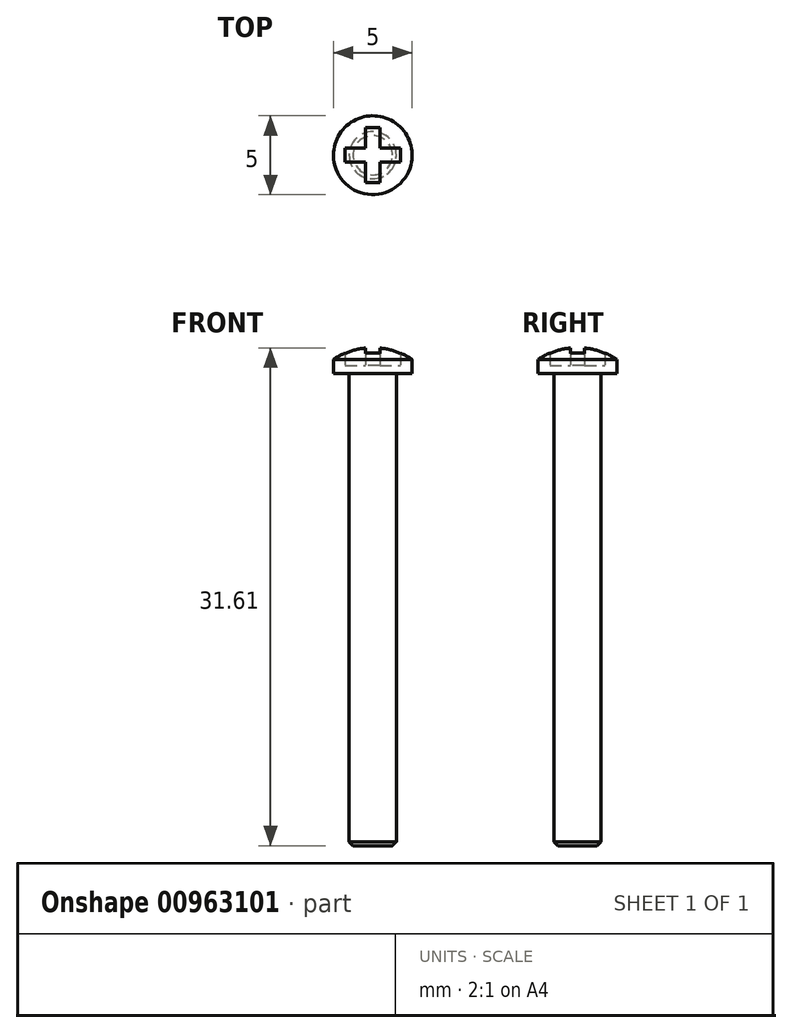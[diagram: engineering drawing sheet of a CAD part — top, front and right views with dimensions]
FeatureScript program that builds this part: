
annotation { "Feature Type Name" : "Feature", "Feature Type Description" : "" }
export const myFeature = defineFeature(function(context is Context, id is Id, definition is map)
    precondition{}
    {
        {
            var Q0;
            Q0=qCreatedBy(makeId("Front.planeOp"),FACE);
            var sketch = newSketch(context, id + "F0", { "sketchPlane" : qUnion([Q0])});
            skLineSegment(sketch, "E0", {"start": v(-1.5, 0) * mm, "end": v(-2.5, 0) * mm});
            skLineSegment(sketch, "E1", {"start": v(-2.5, 0) * mm, "end": v(-2.5, 0.88) * mm});
            skLineSegment(sketch, "E2", {"start": v(-1.5, 0) * mm, "end": v(-1.5, -30) * mm});
            skLineSegment(sketch, "E3", {"start": v(-1.5, -30) * mm, "end": v(0, -30) * mm});
            skLineSegment(sketch, "E4", {"start": v(0, -30) * mm, "end": v(0, 1.66) * mm});
            skArc(sketch, "E5", {"start": v(0, 1.66) * mm, "mid": v(-1.3, 1.46) * mm, "end": v(-2.5, 0.88) * mm});
            skSolve(sketch);
        }
        {
            var Q0;
            Q0 = qSketchRegion(id + "F0", true);
            var Q1;
            Q1=sQuery(id+"F0.wireOp",EDGE,"E4");
            revolve(context, id + "F1", {"surfaceOperationType" : NewSurfaceOperationType.NEW, "entities" : qUnion([Q0]), "axis" : qUnion([Q1]), "revolveType" : RevolveType.FULL});
        }
        {
            var Q0;
            Q0=makeQuery(id+"F1.opRevolve","SWEPT_EDGE",EDGE,{"disambiguationData":[OSD([sQuery(id+"F0.wireOp",EDGE,"E2"),sQuery(id+"F0.wireOp",EDGE,"E3")])]});
            chamfer(context, id + "F2", {"entities" : qUnion([Q0]), "width" : 0.25 * mm, "tangentPropagation" : true});
        }
        {
            var Q0;
            Q0=qCreatedBy(makeId("Top.planeOp"),FACE);
            cPlane(context, id + "F3", {"entities" : qUnion([Q0]), "cplaneType" : CPlaneType.OFFSET, "offset" : 0.5 * mm, "width" : 150 * mm, "height" : 150 * mm});
        }
        {
            var Q0;
            Q0=qCreatedBy(id+"F3.planeOp",FACE);
            var sketch = newSketch(context, id + "F4", { "sketchPlane" : qUnion([Q0])});
            skLineSegment(sketch, "E6.bottom", {"start": v(-1.75, 0.45) * mm, "end": v(-0.45, 0.45) * mm});
            skLineSegment(sketch, "E6.top", {"start": v(-1.75, -0.45) * mm, "end": v(-0.45, -0.45) * mm});
            skLineSegment(sketch, "E6.left", {"start": v(-1.75, 0.45) * mm, "end": v(-1.75, -0.45) * mm});
            skLineSegment(sketch, "E6.right", {"start": v(1.75, 0.45) * mm, "end": v(1.75, -0.45) * mm});
            skLineSegment(sketch, "E7.bottom", {"start": v(0.45, -1.75) * mm, "end": v(-0.45, -1.75) * mm});
            skLineSegment(sketch, "E7.top", {"start": v(0.45, 1.75) * mm, "end": v(-0.45, 1.75) * mm});
            skLineSegment(sketch, "E7.left", {"start": v(0.45, -1.75) * mm, "end": v(0.45, -0.45) * mm});
            skLineSegment(sketch, "E7.right", {"start": v(-0.45, -1.75) * mm, "end": v(-0.45, -0.45) * mm});
            skLineSegment(sketch, "E8", {"start": v(-0.45, 1.75) * mm, "end": v(0.45, -1.75) * mm, "construction": true});
            skLineSegment(sketch, "E9", {"start": v(1.75, 0.45) * mm, "end": v(-1.75, -0.45) * mm, "construction": true});
            skLineSegment(sketch, "E10.trimOffspring", {"start": v(0.45, 0.45) * mm, "end": v(1.75, 0.45) * mm});
            skLineSegment(sketch, "E11.trimOffspring", {"start": v(-0.45, 0.45) * mm, "end": v(-0.45, 1.75) * mm});
            skLineSegment(sketch, "E12.trimOffspring", {"start": v(0.45, -0.45) * mm, "end": v(1.75, -0.45) * mm});
            skLineSegment(sketch, "E13.trimOffspring", {"start": v(0.45, 0.45) * mm, "end": v(0.45, 1.75) * mm});
            skSolve(sketch);
        }
        {
            var Q0;
            Q0 = qSketchRegion(id + "F4", true);
            extrude(context, id + "F5", {"entities" : qUnion([Q0]), "operationType" : NewBodyOperationType.REMOVE, "endBound" : BoundingType.UP_TO_NEXT, "depth" : 25 * mm, "offsetDistance" : 25 * mm});
        }
    });
